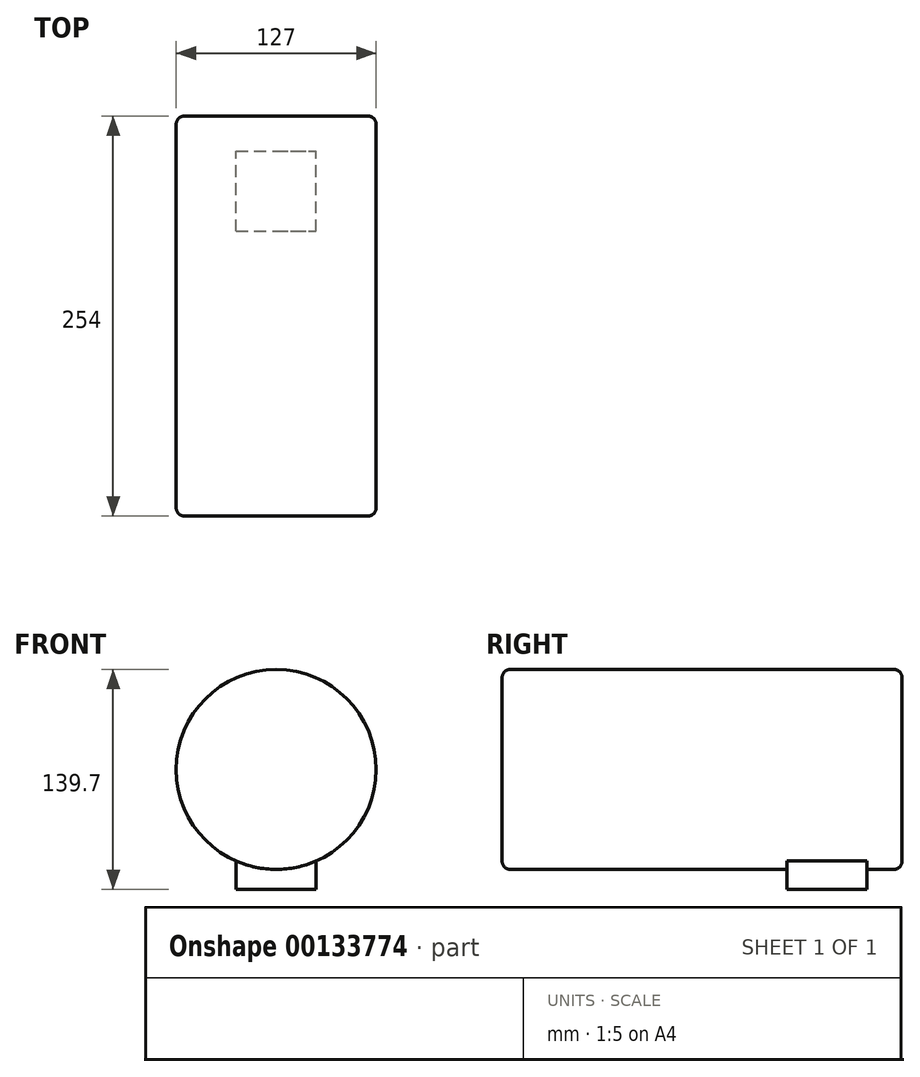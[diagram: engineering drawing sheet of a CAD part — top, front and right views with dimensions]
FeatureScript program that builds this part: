
annotation { "Feature Type Name" : "Feature", "Feature Type Description" : "" }
export const myFeature = defineFeature(function(context is Context, id is Id, definition is map)
    precondition{}
    {
        {
            var Q0;
            Q0=qCreatedBy(makeId("Front.planeOp"),FACE);
            var sketch = newSketch(context, id + "F0", { "sketchPlane" : qUnion([Q0])});
            skCircle(sketch, "E0", {"center": v(0, 0) * mm, "radius": 63.5 * mm});
            skSolve(sketch);
        }
        {
            var Q0;
            Q0=makeQuery(id+"F0.imprint","IMPRINT",FACE,{"disambiguationData":[TD([[makeQuery(id+"F0.imprint","IMPRINT",EDGE,{"derivedFrom":sQuery(id+"F0.wireOp",EDGE,"E0")}),1.0]])]});
            extrude(context, id + "F1", {"entities" : qUnion([Q0]), "depth" : 254 * mm});
        }
        {
            var Q0;
            Q0=makeQuery(id+"F1.opExtrude","CAP_FACE",FACE,{"disambiguationData":[OSD([sQuery(id+"F0.wireOp",EDGE,"E0")])],"isStart":false});
            var sketch = newSketch(context, id + "F2", { "sketchPlane" : qUnion([Q0])});
            skCircle(sketch, "E1", {"center": v(0, 0) * mm, "radius": 12.7 * mm});
            skSolve(sketch);
        }
        {
            var Q0;
            Q0=sQuery(id+"F2.wireOp",EDGE,"E1");
            extrude(context, id + "F3", {"bodyType" : ToolBodyType.SURFACE, "surfaceEntities" : qUnion([Q0]), "depth" : 50.8 * mm});
        }
        {
            var Q0;
            Q0=makeQuery(id+"F1.opExtrude","CAP_EDGE",EDGE,{"disambiguationData":[OSD([sQuery(id+"F0.wireOp",EDGE,"E0")])],"isStart":false});
            var Q1;
            Q1=makeQuery(id+"F1.opExtrude","CAP_EDGE",EDGE,{"disambiguationData":[OSD([sQuery(id+"F0.wireOp",EDGE,"E0")])],"isStart":true});
            fillet(context, id + "F4", {"entities" : qUnion([Q0, Q1]), "radius" : 5.08 * mm, "tangentPropagation" : true, "allowEdgeOverflow" : false});
        }
        {
            var Q0;
            Q0=qCreatedBy(makeId("Top.planeOp"),FACE);
            var sketch = newSketch(context, id + "F5", { "sketchPlane" : qUnion([Q0])});
            skLineSegment(sketch, "E2.bottom", {"start": v(-25.4, -22.36) * mm, "end": v(25.4, -22.36) * mm});
            skLineSegment(sketch, "E2.top", {"start": v(-25.4, -73.16) * mm, "end": v(25.4, -73.16) * mm});
            skLineSegment(sketch, "E2.left", {"start": v(-25.4, -22.36) * mm, "end": v(-25.4, -73.16) * mm});
            skLineSegment(sketch, "E2.right", {"start": v(25.4, -22.36) * mm, "end": v(25.4, -73.16) * mm});
            skPoint(sketch, "E2.middle", {"position": v(0, -47.76) * mm});
            skSolve(sketch);
        }
        {
            var Q0;
            Q0 = qSketchRegion(id + "F5", true);
            extrude(context, id + "F6", {"entities" : qUnion([Q0]), "operationType" : NewBodyOperationType.ADD, "oppositeDirection" : true, "depth" : 76.2 * mm});
        }
    });
